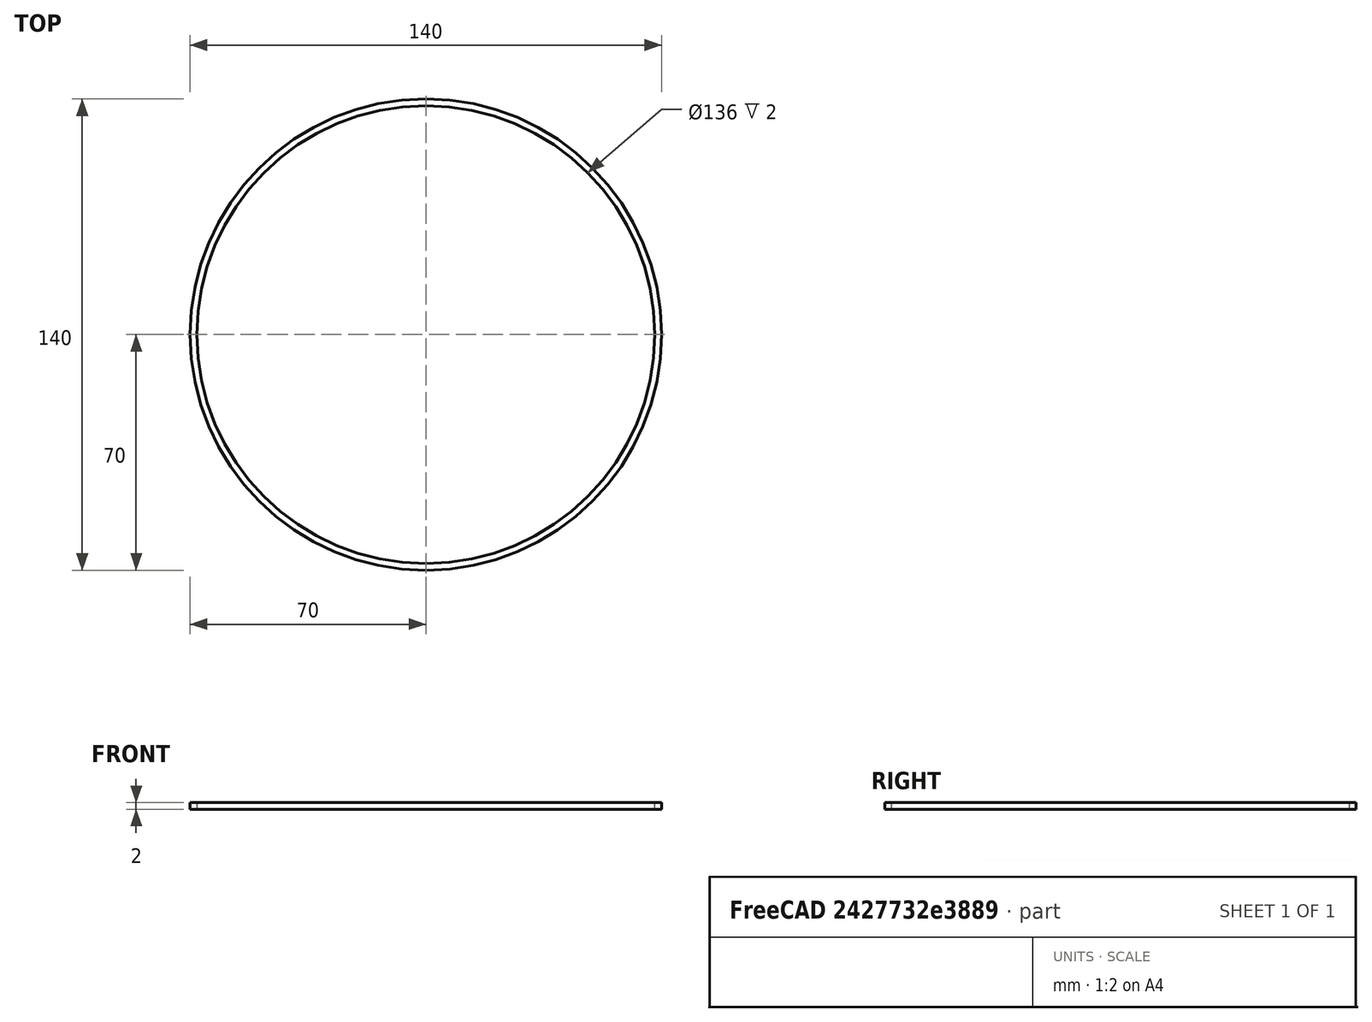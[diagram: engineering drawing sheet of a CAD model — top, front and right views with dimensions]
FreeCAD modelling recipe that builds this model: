
FCSTD DOCUMENT  (FreeCAD 0.18.4R)
Label: кольцоВерх
License: All rights reserved
LicenseURL: http://en.wikipedia.org/wiki/All_rights_reserved
objects: Sketcher::SketchObject×1, PartDesign::Pad×1, PartDesign::Body×1, Mesh::Feature×1
note: 4 computed .brp shape members not serialized (recipe doc carries the construction recipe); baked Part::Feature solids carry a one-line shape summary decoded from their .brp

FEATURE [Sketcher::SketchObject] Sketch
  MapMode = 5
  Support = -> [XY_Plane]
  sketch-geometry (2):
    g0: Circle CenterX=0 CenterY=0 CenterZ=0 NormalX=0 NormalY=0 NormalZ=1 AngleXU=0 Radius=70
    g1: Circle CenterX=0 CenterY=0 CenterZ=0 NormalX=0 NormalY=0 NormalZ=1 AngleXU=0 Radius=68
  constraints (4):
    c: Coincident(g0,g-1)
    c: Coincident(g1,g0)
    c: Diameter(g1) = 136
    c: Diameter(g0) = 140
FEATURE [PartDesign::Pad] Pad
  Length = 2
  Length2 = 100
  Profile = -> Sketch
  Type = 0
FEATURE [PartDesign::Body] Body
  Group = -> [Sketch,Pad]
  Origin = -> Origin
  Tip = -> Pad
FEATURE [Mesh::Feature] Mesh  label="Body (Meshed)"
